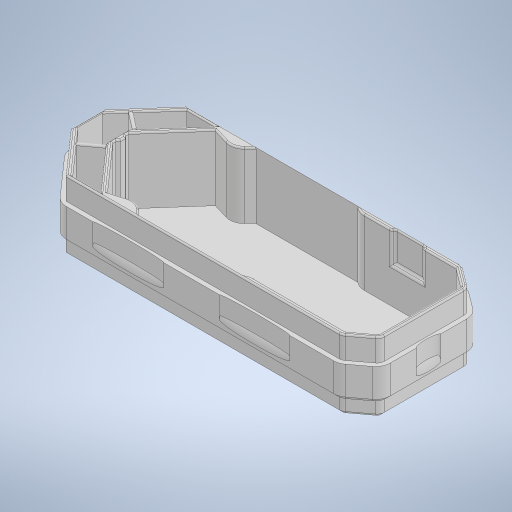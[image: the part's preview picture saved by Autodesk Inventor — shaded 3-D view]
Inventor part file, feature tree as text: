
AUTODESK INVENTOR PART (.ipt)
format: ipt  version: 2024.1 (Build 281209000, 209)  size: 1,604,096 bytes
history: native  units: mm
features: extrude x18, sketch x18, projected_geometry x18, fillet x13, chamfer x4, other x2, plane x2, mirror x1, pattern_circular x1
ambient origin geometry x8: Origin, YZ Plane, XZ Plane, XY Plane, X Axis, Y Axis, Z Axis, Center Point
bodies: Solid1 (feature_tree), Solid2 (feature_tree)
feature tree (77):
  extrude  "44mm-body"  Depth=3.0mm TaperAngle=0.0deg
  extrude  "Extrusion2"  Depth=3.0mm
  extrude  "Extrusion3"  Depth=3.0mm
  extrude  "Extrusion8"  Depth=32.0mm TaperAngle=0.0deg
  extrude  "Extrusion10"  Depth=4.0mm TaperAngle=0.0deg
  extrude  "Extrusion4"  Depth=10.0mm
  extrude  "Extrusion11"  Depth=10.0mm
  extrude  "Extrusion5"  Depth=10.0mm
  extrude  "Extrusion6"  Depth=4.0mm TaperAngle=45.0deg
  fillet  "Fillet1"  Radius=3.0mm
  fillet  "Fillet2"  Radius=3.0mm
  fillet  "Fillet3"  Radius=12.4mm
  fillet  "Fillet4"  Radius=55.0mm
  extrude  "Extrusion7"  Depth=9.25mm
  fillet  "Fillet5"  Radius=3.4mm
  other  "Work Axis1"
  mirror  "Mirror1"
  pattern_circular  "Circular Pattern1"  [2 undecoded]
  chamfer  "Chamfer1"  Distance=8.0mm
  chamfer  "Chamfer2"  Distance=8.0mm
  extrude  "Extrusion12"  Depth=0.4mm
  extrude  "Extrusion13"  Depth=0.4mm
  extrude  "Extrusion14"  Depth=0.4mm
  extrude  "Extrusion15"  Depth=0.4mm
  extrude  "Extrusion16"  Depth=0.4mm
  fillet  "Fillet6"  Radius=1.5mm
  extrude  "Extrusion17"  Depth=0.4mm
  extrude  "Extrusion18"  Depth=0.4mm
  fillet  "Fillet7"  Radius=14.3mm
  fillet  "Fillet8"  Radius=49.0mm
  extrude  "Extrusion19"  Depth=0.4mm
  chamfer  "Chamfer3"  Distance=49.0mm
  fillet  "Fillet9"  Radius=3.0mm
  chamfer  "Chamfer4"  Distance=3.0mm
  fillet  "Fillet11"  Radius=2.5mm
  fillet  "Fillet10"  Radius=22.0mm
  fillet  "Fillet12"  Radius=2.0mm
  fillet  "Fillet13"  Radius=1.5mm
  sketch  "Sketch1"  dims[d4=44.0mm d5=0.0mm d6=3.0mm d7=0.0mm]
  sketch  "Sketch2"  dims[d44=3.0mm d45=3.0mm]
  projected_geometry  "Projected Loop1"
  sketch  "Sketch3"  dims[d46=3.0mm d47=3.0mm]
  projected_geometry  "Projected Loop2"
  sketch  "Sketch4"  dims[d48=0.0mm d49=0.0mm d53=32.0mm d54=0.0mm]
  projected_geometry  "Projected Loop3"
  sketch  "Sketch5"  dims[d55=16.0mm d56=0.0mm d57=4.0mm d58=0.0mm]
  projected_geometry  "Projected Loop4"
  sketch  "Sketch6"  dims[d59=5.0mm d60=10.0mm]
  projected_geometry  "Projected Loop5"
  sketch  "Sketch7"  dims[d61=10.0mm d62=10.0mm]
  plane  "Work Plane1"
  plane  "Work Plane2"
  sketch  "Sketch8"  dims[d63=12.0mm d64=0.0mm d65=10.0mm]
  sketch  "Sketch11"  dims[d66=20.0mm d67=360.0deg d69=4.0mm d70=2.0mm d71=45.0deg]
  sketch  "Sketch13"  dims[d72=4.0mm d73=2.0mm d74=45.0deg d75=3.0mm d76=3.0mm d77=12.4mm d78=55.0mm]
  projected_geometry  "Projected Loop6"
  sketch  "Sketch14"  dims[d79=9.25mm d80=9.25mm d81=3.4mm]
  sketch  "Sketch15"  dims[d82=3.4mm]
  projected_geometry  "Projected Loop7"
  sketch  "Sketch16"  dims[d83=80.4mm]
  projected_geometry  "Projected Loop8"
  projected_geometry  "Projected Loop9"
  projected_geometry  "Projected Loop10"
  projected_geometry  "Projected Loop11"
  other  "battery"
  sketch  "Sketch17"  dims[d84=136.0mm]
  projected_geometry  "Projected Loop12"
  projected_geometry  "Projected Loop13"
  projected_geometry  "Projected Loop14"
  projected_geometry  "Projected Loop15"
  sketch  "Sketch18"  dims[d85=2.5mm]
  projected_geometry  "Projected Loop16"
  projected_geometry  "Projected Loop17"
  sketch  "Sketch19"  dims[d87=2.5mm]
  sketch  "Sketch20"  dims[d88=8.0mm]
  sketch  "Sketch22"  dims[d89=14.0mm d90=198.0mm d91=8.0mm d92=8.0mm d93=16.0mm d94=72.0mm d95=80.3mm d96=33.15mm d97=4.15mm d98=1.5mm d99=2.0mm d100=2.0mm d101=14.3mm d102=49.0mm d103=14.3mm d104=49.0mm d105=3.0mm d106=3.0mm d107=2.5mm d108=22.0mm d109=0.0mm d121=2.0mm d122=1.5mm d123=14.2mm d124=3.1mm d125=2.0mm d126=14.2mm d127=18.25mm d128=0.0mm d129=3.0mm d130=3.0mm d131=3.0mm d132=3.0mm d133=3.0mm d134=32.0mm d135=0.0mm d136=0.1mm d137=0.0mm d138=14.2mm d139=2.0mm d140=0.0mm d141=50.2mm d142=0.0mm d143=16.0mm d144=3.0mm d145=0.0mm d146=6.5mm d147=0.5mm d148=0.0mm d149=2.0mm d153=2.0mm d154=2.0mm d155=0.5mm d156=0.0mm d157=23.0mm d158=20.0mm d159=1.5mm d160=20.0mm d161=0.0mm d162=2.0mm d163=1.0mm d164=1.0mm d165=10.0mm d166=0.0mm d167=2.5mm d168=2.0mm d169=45.0deg d170=3.0mm d171=2.0mm d172=45.0deg d173=1.736086mm d174=67.0mm d175=47.137037mm d176=43.431481mm d177=1.321163mm d178=23.568519mm d179=8.479885mm d180=8.0mm d181=1.0mm d182=10.0mm d183=0.9mm d184=0.4mm]
  projected_geometry  "Projected Loop18"
note: 2 required parameter values undecoded (feature->parameter linkage not recoverable at this tier; creation-order binding heuristic only, values carry confidence <= 0.55)
